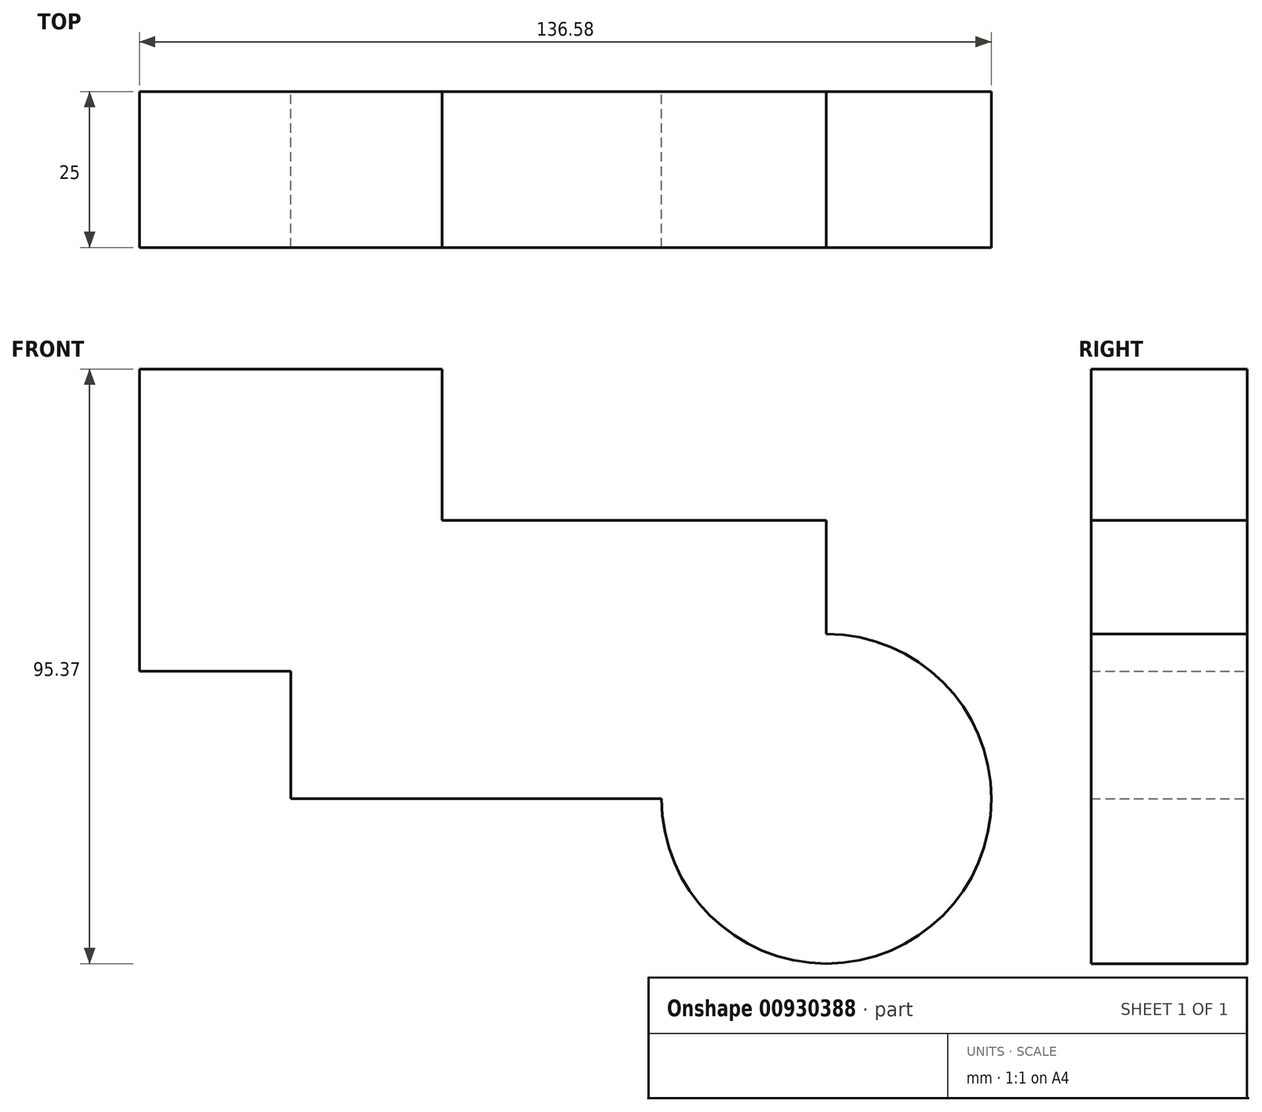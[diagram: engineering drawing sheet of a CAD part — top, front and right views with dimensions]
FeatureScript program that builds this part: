
annotation { "Feature Type Name" : "Feature", "Feature Type Description" : "" }
export const myFeature = defineFeature(function(context is Context, id is Id, definition is map)
    precondition{}
    {
        {
            var Q0;
            Q0=qCreatedBy(makeId("Front.planeOp"),FACE);
            var sketch = newSketch(context, id + "F0", { "sketchPlane" : qUnion([Q0])});
            skLineSegment(sketch, "E0.bottom", {"start": v(-133.53, 28.6) * mm, "end": v(-47.63, 28.6) * mm});
            skLineSegment(sketch, "E0.top", {"start": v(-133.53, -16.08) * mm, "end": v(-47.63, -16.08) * mm});
            skLineSegment(sketch, "E0.left", {"start": v(-133.53, 28.6) * mm, "end": v(-133.53, -16.08) * mm});
            skLineSegment(sketch, "E0.right", {"start": v(-47.63, 28.6) * mm, "end": v(-47.63, -16.08) * mm});
            skCircle(sketch, "E1.cCircle", {"center": v(-133.53, 28.6) * mm, "radius": 24.25 * mm});
            skLineSegment(sketch, "E1.0", {"start": v(-157.77, 52.85) * mm, "end": v(-109.28, 52.85) * mm});
            skLineSegment(sketch, "E1.1", {"start": v(-109.28, 52.85) * mm, "end": v(-109.28, 4.35) * mm});
            skLineSegment(sketch, "E1.2", {"start": v(-109.28, 4.35) * mm, "end": v(-157.77, 4.35) * mm});
            skLineSegment(sketch, "E1.3", {"start": v(-157.77, 4.35) * mm, "end": v(-157.77, 52.85) * mm});
            skPoint(sketch, "E1.0.midPoint", {"position": v(-133.53, 52.85) * mm});
            skCircle(sketch, "E2", {"center": v(-47.63, -16.08) * mm, "radius": 26.44 * mm});
            skSolve(sketch);
        }
        {
            var Q0;
            Q0 = qSketchRegion(id + "F0", true);
            extrude(context, id + "F1", {"entities" : qUnion([Q0]), "depth" : 25 * mm, "offsetDistance" : 25 * mm});
        }
    });
